# Revit family: Cabrio Base
name_source: partatom
category: Mechanical Equipment
units: mm (PartAtom-declared; Revit-internal decimal feet)

## family parameters
Always vertical = Yes
Classification = None
Cut with Voids When Loaded = No
Part Type = Normal
Room Calculation Point = No
Round Connector Dimension = Use Diameter
Shared = No
Work Plane-Based = No

## types (4) — shared parameters
00_20_Manufacturer = Blauberg
00_20_Name = Extraction fan
Amperage = 0 A
Apparent Load = 14 W
Casing Material = Plastic, opaque, white
Description = For round channels
Diameter = 99 mm  [stored 0.324803 ft]
Dy = 94 mm  [stored 0.308399 ft]
Height = 221 mm  [stored 0.725066 ft]
Length = 116 mm  [stored 0.380577 ft]
Load Classification = HVAC
Maintenance zone material = <By Category>
Manufacturer = Blauberg
Maximum Air Flow = 97.0 m³/h
Number of Fase = 1
Power = 9 W
Sound pressure level at 3 m distance = 25 dBA
URL = https://blaubergventilatoren.de
Voltage = 230 V
Weight = 0.55 kg
Width = 175 mm  [stored 0.574147 ft]
a = 175 mm  [stored 0.574147 ft]
b = 221 mm  [stored 0.725066 ft]
c = 77 mm  [stored 0.252625 ft]
d = 99 mm  [stored 0.324803 ft]
e = 39 mm  [stored 0.127953 ft]
zero-valued in all types: Default Elevation

## per-type parameters (varying)
| type | Frequency |
| Cabrio Base 100 T | 50 Hz |
| Cabrio Base 100 T (220-240V/60Hz) | 60 Hz |
| Cabrio Base 100 H | 50 Hz |
| Cabrio Base 100 H (220-240V/60Hz) | 60 Hz |

note: column(s) folded — value = type name in every type: 00_20_Type

note: [stored X ft] marks values corroborated as IEEE doubles in the binary element streams (Revit-internal decimal feet)
